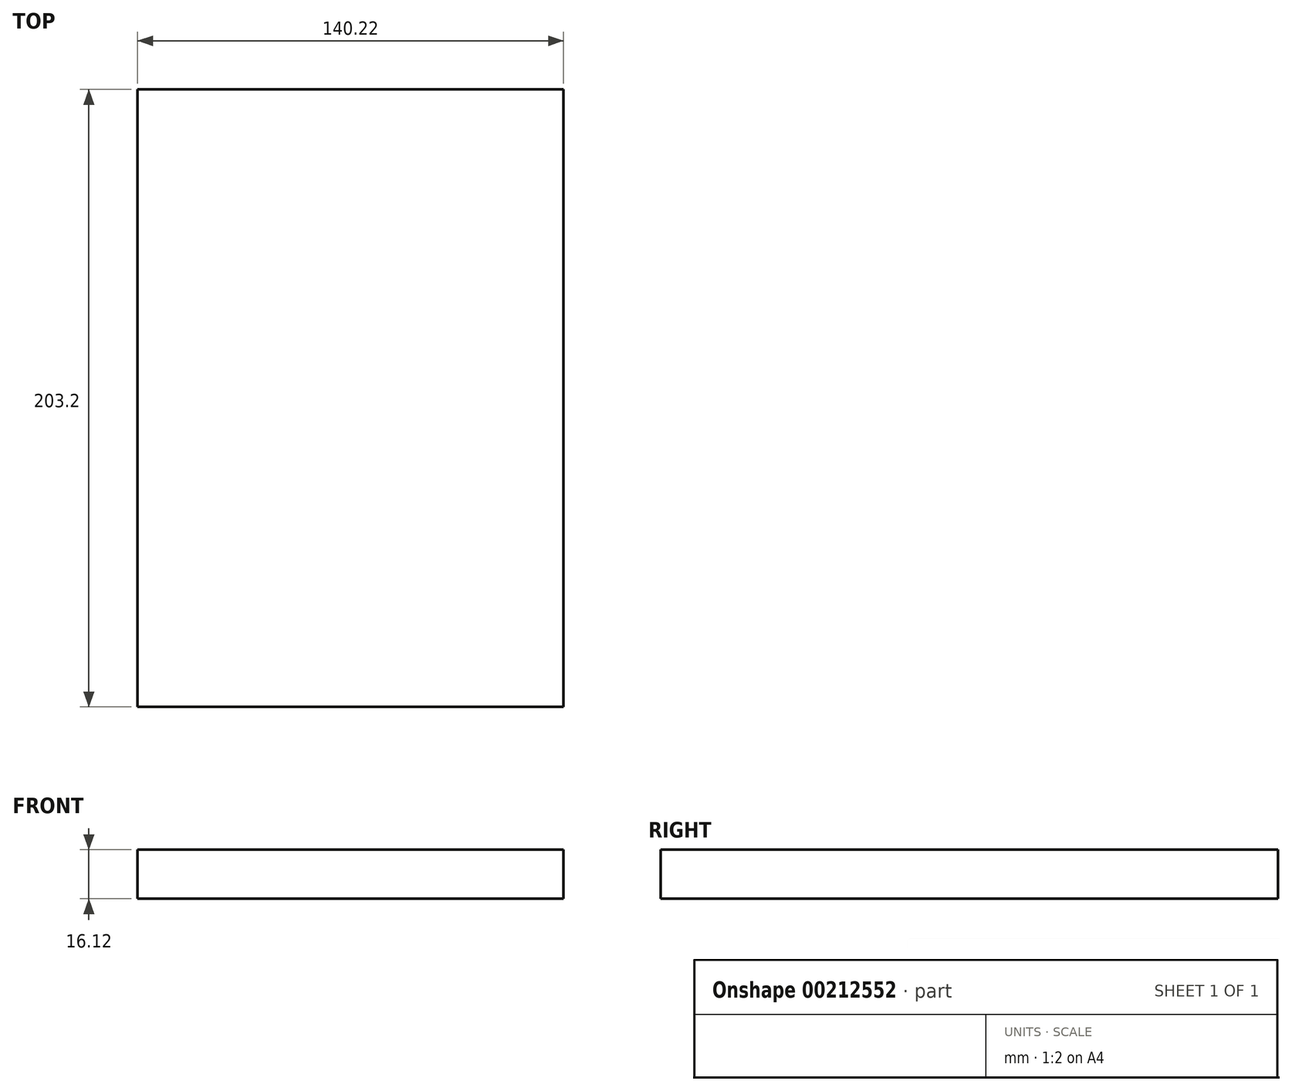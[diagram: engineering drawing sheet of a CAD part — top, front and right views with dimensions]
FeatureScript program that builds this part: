
annotation { "Feature Type Name" : "Feature", "Feature Type Description" : "" }
export const myFeature = defineFeature(function(context is Context, id is Id, definition is map)
    precondition{}
    {
        {
            var Q0;
            Q0=qCreatedBy(makeId("Front.planeOp"),FACE);
            var sketch = newSketch(context, id + "F0", { "sketchPlane" : qUnion([Q0])});
            skLineSegment(sketch, "E0.bottom", {"start": v(-70.1, 40.18) * mm, "end": v(70.1, 40.18) * mm});
            skLineSegment(sketch, "E0.top", {"start": v(-70.1, 56.3) * mm, "end": v(70.1, 56.3) * mm});
            skLineSegment(sketch, "E0.left", {"start": v(-70.1, 40.18) * mm, "end": v(-70.1, 56.3) * mm});
            skLineSegment(sketch, "E0.right", {"start": v(70.1, 40.18) * mm, "end": v(70.1, 56.3) * mm});
            skPoint(sketch, "E0.middle", {"position": v(0, 48.24) * mm});
            skSolve(sketch);
        }
        {
            var Q0;
            Q0 = qSketchRegion(id + "F0", true);
            extrude(context, id + "F1", {"entities" : qUnion([Q0]), "depth" : 101.6 * mm, "hasSecondDirection" : true, "secondDirectionOppositeDirection" : true, "secondDirectionDepth" : 101.6 * mm});
        }
    });
